# Revit family: Sink-Undermount-Lavatory-KOHLER-Caxton_Oval-K-2210LM_1
name_source: partatom
category: Plumbing Fixtures
revit_build: Autodesk Revit 2017 (Build: 20160225_1515(x64)
units: mm (PartAtom-declared; Revit-internal decimal feet)

## family parameters
Cut with Voids When Loaded = No
Host = Face
OmniClass Number = 23.31.13.00
OmniClass Title = Sinks
Part Type = Normal
Room Calculation Point = No
Round Connector Dimension = Use Diameter
Shared = No

## types (1)
- 0-White
    ADA Compliant = No
    Assembly Code = D2010400
    CW Connection = No
    Cold Water Inlet = Cold Water Inlet
    Date Modified = 06/23/2020
    Default Elevation = 36"
    Description = Undercounter Mount Sink
    Drain Included = No
    Finish = Kohler-Vitreous_China-0-White
    HW Connection = No
    Height = 7 1/2"
    Hot Water Inlet = Hot Water Inlet
    Length = 19 1/4"
    Manufacturer = KOHLER Co.
    Master Format 2014 = 22.41.16
    Master Format 2014 Name = Residential Lavatories and Sinks
    Material = Vitreous China
    Model = K-2210LM-0
    Product Documentation Link = http://resources.kohler.com
    Product Name = Caxton Oval
    Product Page URL = https://la.kohler.com
    URL = https://la.kohler.com
    Vent Connection = No
    Waste Connection = Yes
    Waste Water Outlet = Waste Water Outlet
    WaterSense Certified = No
    Width = 16 1/4"

## geometry (parser evidence)
native form markers: Sweep x3
no freeform markers — native parametric forms only
